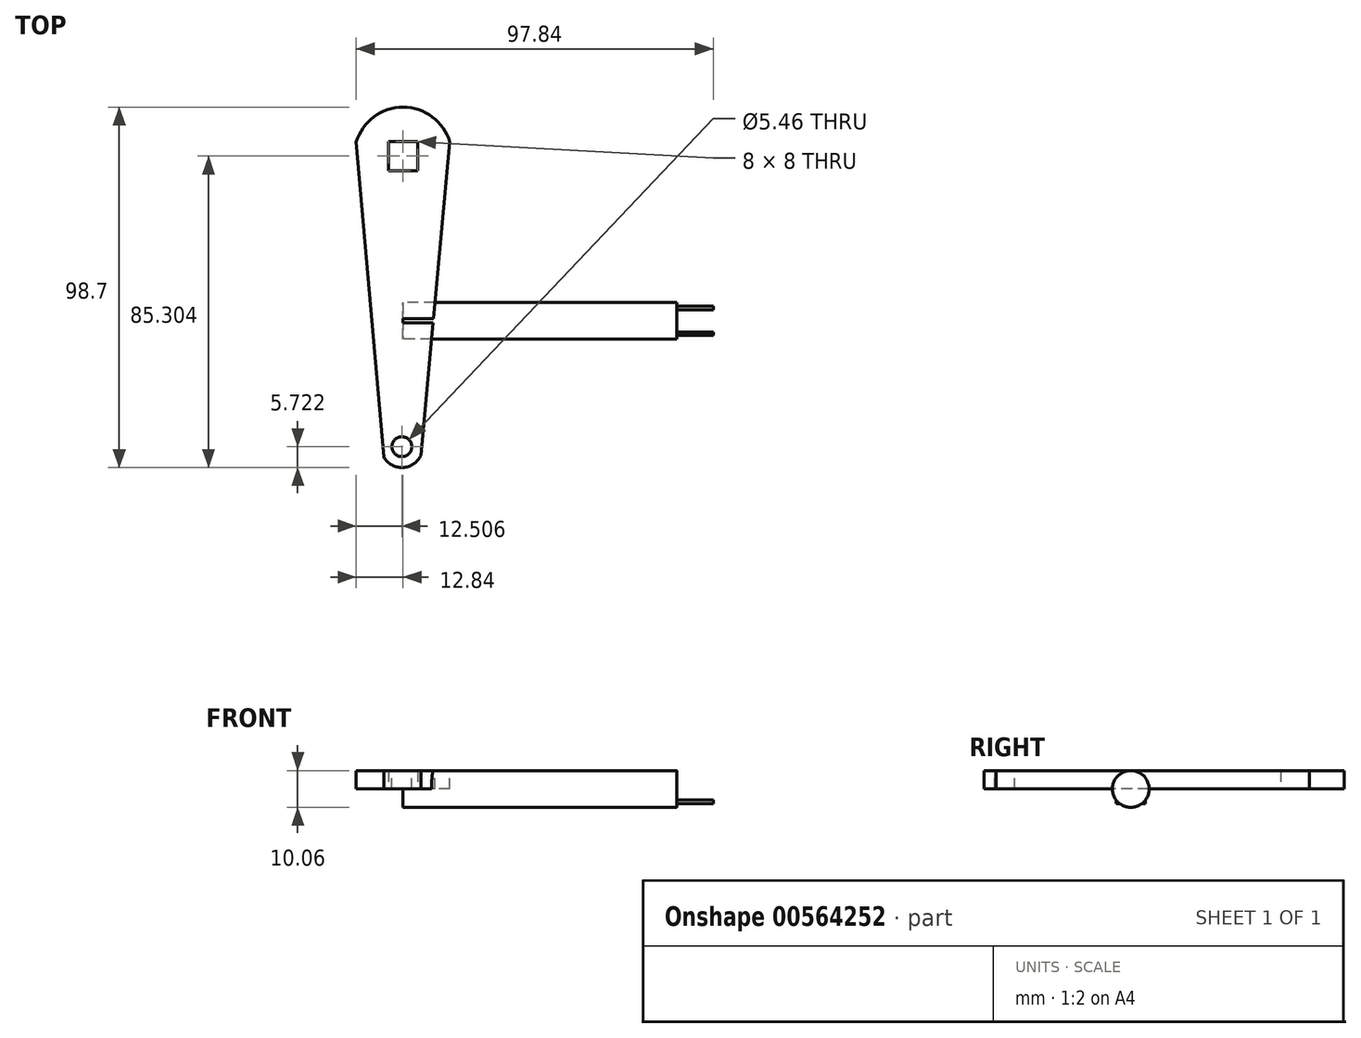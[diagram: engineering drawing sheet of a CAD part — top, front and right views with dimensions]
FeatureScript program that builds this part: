
annotation { "Feature Type Name" : "Feature", "Feature Type Description" : "" }
export const myFeature = defineFeature(function(context is Context, id is Id, definition is map)
    precondition{}
    {
        {
            var Q0;
            Q0=qCreatedBy(makeId("Right.planeOp"),FACE);
            var sketch = newSketch(context, id + "F0", { "sketchPlane" : qUnion([Q0])});
            skCircle(sketch, "E0", {"center": v(0, 0) * mm, "radius": 5.03 * mm});
            skSolve(sketch);
        }
        {
            var Q0;
            Q0=makeQuery(id+"F0.imprint","IMPRINT",FACE,{"disambiguationData":[TD([[makeQuery(id+"F0.imprint","IMPRINT",EDGE,{"derivedFrom":sQuery(id+"F0.wireOp",EDGE,"E0")}),1.0]])]});
            extrude(context, id + "F1", {"entities" : qUnion([Q0]), "depth" : 75 * mm, "offsetDistance" : 25 * mm});
        }
        {
            var Q0;
            Q0=makeQuery(id+"F1.opExtrude","CAP_FACE",FACE,{"disambiguationData":[OSD([sQuery(id+"F0.wireOp",EDGE,"E0")])],"isStart":false});
            var sketch = newSketch(context, id + "F2", { "sketchPlane" : qUnion([Q0])});
            skSolve(sketch);
        }
        {
            var Q0;
            Q0=qCreatedBy(makeId("Top.planeOp"),FACE);
            var sketch = newSketch(context, id + "F3", { "sketchPlane" : qUnion([Q0])});
            skArc(sketch, "E1", {"start": v(12.83, 48.95) * mm, "mid": v(0, 58.5) * mm, "end": v(-12.83, 48.95) * mm});
            skArc(sketch, "E2", {"start": v(-5.31, -37.3) * mm, "mid": v(-0.09, -40.2) * mm, "end": v(4.87, -36.85) * mm});
            skFitSpline(sketch, "E3", {"points": [v(12.83, 48.95) * mm, v(4.87, -36.85) * mm], "startDerivative": vector(-7.97, -85.86) * mm, "endDerivative": vector(-7.97, -85.86) * mm});
            skFitSpline(sketch, "E4", {"points": [v(-12.83, 48.95) * mm, v(-5.31, -37.3) * mm], "startDerivative": vector(7.52, -86.3) * mm, "endDerivative": vector(7.52, -86.3) * mm});
            skLineSegment(sketch, "E5.bottom", {"start": v(4, 41.1) * mm, "end": v(-4, 41.1) * mm});
            skLineSegment(sketch, "E5.top", {"start": v(4, 49.1) * mm, "end": v(-4, 49.1) * mm});
            skLineSegment(sketch, "E5.left", {"start": v(4, 41.1) * mm, "end": v(4, 49.1) * mm});
            skLineSegment(sketch, "E5.right", {"start": v(-4, 41.1) * mm, "end": v(-4, 49.1) * mm});
            skSolve(sketch);
        }
        {
            var Q0;
            Q0=makeQuery(id+"F3.imprint","IMPRINT",FACE,{"disambiguationData":[TD([[makeQuery(id+"F3.imprint","IMPRINT",EDGE,{"derivedFrom":sQuery(id+"F3.wireOp",EDGE,"E1")}),1.0]])]});
            extrude(context, id + "F4", {"entities" : qUnion([Q0]), "operationType" : NewBodyOperationType.ADD, "depth" : 5 * mm, "offsetDistance" : 25 * mm});
        }
        {
            var Q0;
            Q0=makeQuery(id+"F2.imprint","IMPRINT",FACE,{"disambiguationData":[TD([[makeQuery(id+"F2.imprint","IMPRINT",EDGE,{"derivedFrom":makeQuery(id+"F1.opExtrude","CAP_EDGE",EDGE,{"disambiguationData":[OSD([sQuery(id+"F0.wireOp",EDGE,"E0")])],"isStart":false})}),1.0]])]});
            var sketch = newSketch(context, id + "F5", { "sketchPlane" : qUnion([Q0])});
            skLineSegment(sketch, "E6.bottom", {"start": v(4, -4) * mm, "end": v(-4, -4) * mm});
            skLineSegment(sketch, "E6.top", {"start": v(4, 4) * mm, "end": v(-4, 4) * mm});
            skLineSegment(sketch, "E6.left", {"start": v(4, -4) * mm, "end": v(4, 4) * mm});
            skLineSegment(sketch, "E6.right", {"start": v(-4, -4) * mm, "end": v(-4, 4) * mm});
            skPoint(sketch, "E6.middle", {"position": v(0, 0) * mm});
            skSolve(sketch);
        }
        {
            var Q0;
            Q0=makeQuery(id+"F5.imprint","IMPRINT",FACE,{"disambiguationData":[TD([[makeQuery(id+"F5.imprint","IMPRINT",EDGE,{"derivedFrom":sQuery(id+"F5.wireOp",EDGE,"E6.bottom")}),-1.0]])]});
            extrude(context, id + "F6", {"entities" : qUnion([Q0]), "operationType" : NewBodyOperationType.ADD, "depth" : 10 * mm, "offsetDistance" : 25 * mm});
        }
        {
            var Q0;
            Q0=makeQuery(id+"F4.opExtrude","CAP_FACE",FACE,{"disambiguationData":[OSD([sQuery(id+"F3.wireOp",EDGE,"E1"),sQuery(id+"F3.wireOp",EDGE,"E2"),sQuery(id+"F3.wireOp",EDGE,"E3"),sQuery(id+"F3.wireOp",EDGE,"E4"),sQuery(id+"F3.wireOp",EDGE,"E5.bottom"),sQuery(id+"F3.wireOp",EDGE,"E5.top"),sQuery(id+"F3.wireOp",EDGE,"E5.left"),sQuery(id+"F3.wireOp",EDGE,"E5.right")])],"isStart":false});
            var sketch = newSketch(context, id + "F7", { "sketchPlane" : qUnion([Q0])});
            skCircle(sketch, "E7", {"center": v(-0.33, -34.48) * mm, "radius": 2.73 * mm});
            skSolve(sketch);
        }
        {
            var Q0;
            Q0=makeQuery(id+"F7.imprint","IMPRINT",FACE,{"disambiguationData":[TD([[makeQuery(id+"F7.imprint","IMPRINT",EDGE,{"derivedFrom":sQuery(id+"F7.wireOp",EDGE,"E7")}),1.0]])]});
            extrude(context, id + "F8", {"entities" : qUnion([Q0]), "operationType" : NewBodyOperationType.REMOVE, "oppositeDirection" : true, "depth" : 25 * mm, "offsetDistance" : 25 * mm});
        }
    });
